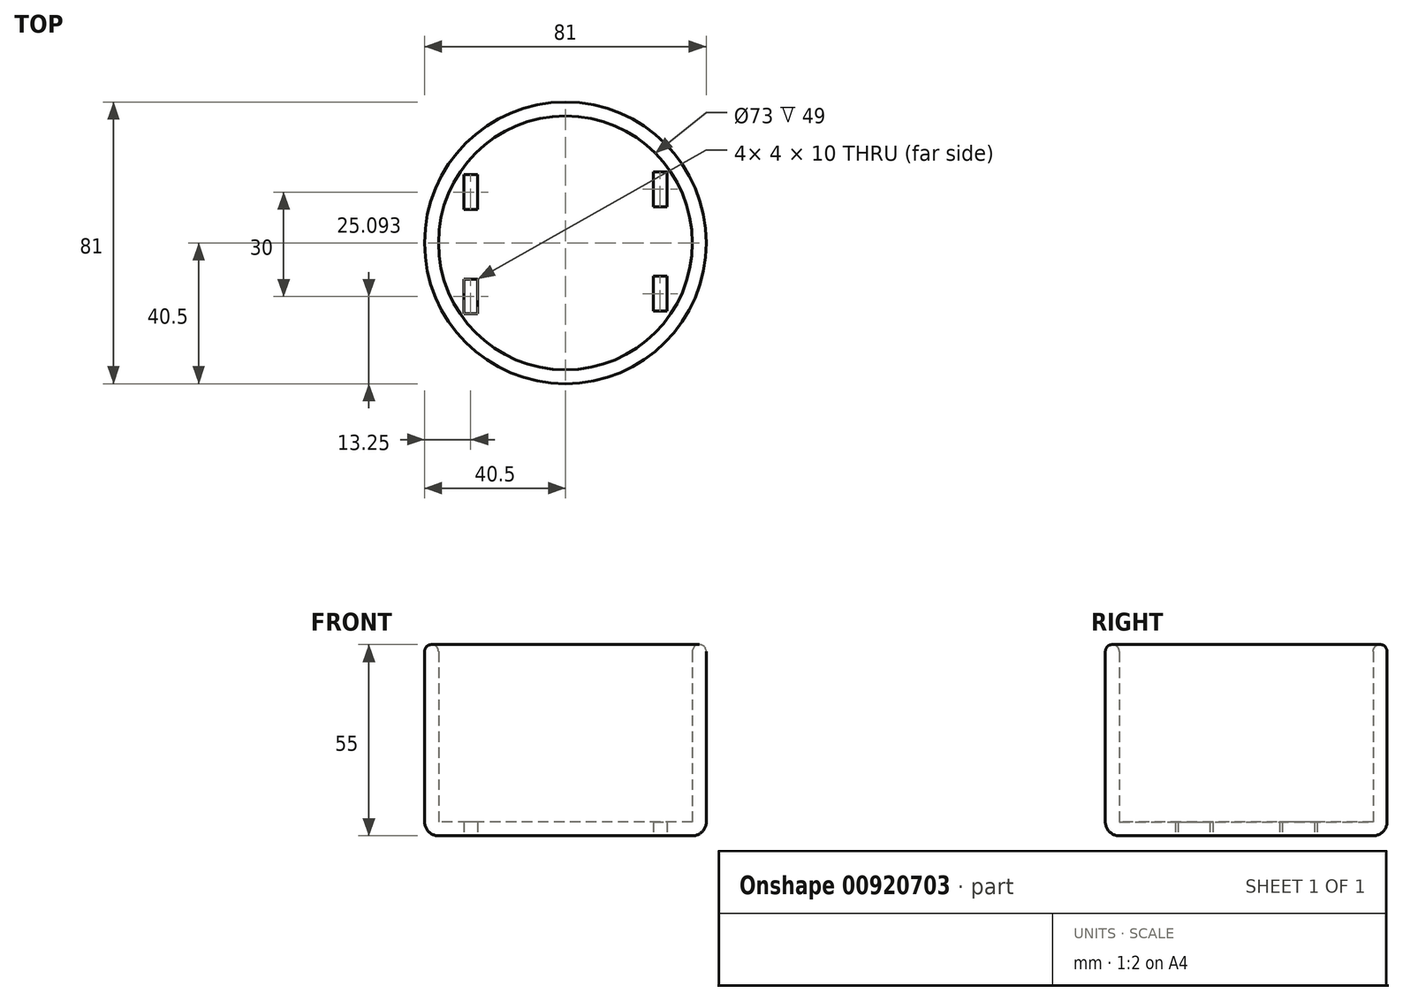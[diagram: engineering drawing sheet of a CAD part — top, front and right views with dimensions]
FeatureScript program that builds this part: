
annotation { "Feature Type Name" : "Feature", "Feature Type Description" : "" }
export const myFeature = defineFeature(function(context is Context, id is Id, definition is map)
    precondition{}
    {
        {
            var Q0;
            Q0=qCreatedBy(makeId("Top.planeOp"),FACE);
            var sketch = newSketch(context, id + "F0", { "sketchPlane" : qUnion([Q0])});
            skCircle(sketch, "E0", {"center": v(0, 0) * mm, "radius": 36.5 * mm});
            skCircle(sketch, "E1", {"center": v(0, 0) * mm, "radius": 40.5 * mm});
            skLineSegment(sketch, "E2.left", {"start": v(25.25, -19.6) * mm, "end": v(25.25, -9.6) * mm});
            skLineSegment(sketch, "E3.bottom", {"start": v(-25.25, 19.6) * mm, "end": v(-25.25, 19.6) * mm});
            skLineSegment(sketch, "E3.top", {"start": v(-25.25, -20.4) * mm, "end": v(-25.25, -20.4) * mm});
            skLineSegment(sketch, "E3.left", {"start": v(-25.25, 19.6) * mm, "end": v(-25.25, 9.6) * mm});
            skLineSegment(sketch, "E3.right", {"start": v(-25.25, 19.6) * mm, "end": v(-25.25, 9.6) * mm});
            skLineSegment(sketch, "E4.bottom", {"start": v(-25.25, 19.6) * mm, "end": v(-29.25, 19.6) * mm});
            skLineSegment(sketch, "E4.top", {"start": v(-25.25, -20.4) * mm, "end": v(-29.25, -20.4) * mm});
            skLineSegment(sketch, "E4.right", {"start": v(-29.25, 19.6) * mm, "end": v(-29.25, 9.6) * mm});
            skLineSegment(sketch, "E5.bottom", {"start": v(25.25, 20.4) * mm, "end": v(29.25, 20.4) * mm});
            skLineSegment(sketch, "E5.top", {"start": v(25.25, -19.6) * mm, "end": v(29.25, -19.6) * mm});
            skLineSegment(sketch, "E5.left", {"start": v(25.25, 20.4) * mm, "end": v(25.25, 10.4) * mm});
            skLineSegment(sketch, "E5.right", {"start": v(29.25, 20.4) * mm, "end": v(29.25, 10.4) * mm});
            skLineSegment(sketch, "E6.bottom", {"start": v(-29.25, -20.4) * mm, "end": v(-25.25, -20.4) * mm});
            skLineSegment(sketch, "E6.top", {"start": v(-29.25, -10.4) * mm, "end": v(-25.25, -10.4) * mm});
            skLineSegment(sketch, "E6.left", {"start": v(-29.25, -20.4) * mm, "end": v(-29.25, -10.4) * mm});
            skLineSegment(sketch, "E6.right", {"start": v(-25.25, -20.4) * mm, "end": v(-25.25, -10.4) * mm});
            skLineSegment(sketch, "E7.bottom", {"start": v(-29.25, 19.6) * mm, "end": v(-25.25, 19.6) * mm});
            skLineSegment(sketch, "E7.top", {"start": v(-29.25, 9.6) * mm, "end": v(-25.25, 9.6) * mm});
            skLineSegment(sketch, "E8.bottom", {"start": v(29.25, 20.4) * mm, "end": v(25.25, 20.4) * mm});
            skLineSegment(sketch, "E8.top", {"start": v(29.25, 10.4) * mm, "end": v(25.25, 10.4) * mm});
            skLineSegment(sketch, "E9.bottom", {"start": v(29.25, -19.6) * mm, "end": v(25.25, -19.6) * mm});
            skLineSegment(sketch, "E9.top", {"start": v(29.25, -9.6) * mm, "end": v(25.25, -9.6) * mm});
            skLineSegment(sketch, "E9.left", {"start": v(29.25, -19.6) * mm, "end": v(29.25, -9.6) * mm});
            skLineSegment(sketch, "E10.trimOffspring", {"start": v(-29.25, -10.4) * mm, "end": v(-29.25, -20.4) * mm});
            skLineSegment(sketch, "E11.trimOffspring", {"start": v(25.25, -9.6) * mm, "end": v(25.25, -19.6) * mm});
            skLineSegment(sketch, "E12.trimOffspring", {"start": v(29.25, -9.6) * mm, "end": v(29.25, -19.6) * mm});
            skLineSegment(sketch, "E13.trimOffspring", {"start": v(25.25, 10.4) * mm, "end": v(25.25, 20.4) * mm});
            skSolve(sketch);
        }
        {
            var Q0;
            Q0=makeQuery(id+"F0.imprint","IMPRINT",FACE,{"disambiguationData":[TD([[makeQuery(id+"F0.imprint","IMPRINT",EDGE,{"derivedFrom":sQuery(id+"F0.wireOp",EDGE,"E0")}),1.0]])]});
            extrude(context, id + "F1", {"entities" : qUnion([Q0]), "depth" : 4 * mm, "offsetDistance" : 25 * mm});
        }
        {
            var Q0;
            Q0=makeQuery(id+"F0.imprint","IMPRINT",FACE,{"disambiguationData":[TD([[makeQuery(id+"F0.imprint","IMPRINT",EDGE,{"derivedFrom":sQuery(id+"F0.wireOp",EDGE,"E0")}),-1.0]])]});
            extrude(context, id + "F2", {"entities" : qUnion([Q0]), "operationType" : NewBodyOperationType.ADD, "depth" : 55 * mm, "offsetDistance" : 25 * mm});
        }
        {
            var Q0;
            Q0=makeQuery(id+"F2.opExtrude","CAP_FACE",FACE,{"disambiguationData":[OSD([sQuery(id+"F0.wireOp",EDGE,"E0"),sQuery(id+"F0.wireOp",EDGE,"E1")])],"isStart":false});
            fillet(context, id + "F3", {"entities" : qUnion([Q0]), "radius" : 2 * mm, "tangentPropagation" : true, "allowEdgeOverflow" : false});
        }
        {
            var Q0;
            Q0=makeQuery(id+"F2.opExtrude","CAP_EDGE",EDGE,{"disambiguationData":[OSD([sQuery(id+"F0.wireOp",EDGE,"E1")])],"isStart":true});
            fillet(context, id + "F4", {"entities" : qUnion([Q0]), "radius" : 4 * mm, "tangentPropagation" : true, "allowEdgeOverflow" : false});
        }
    });
